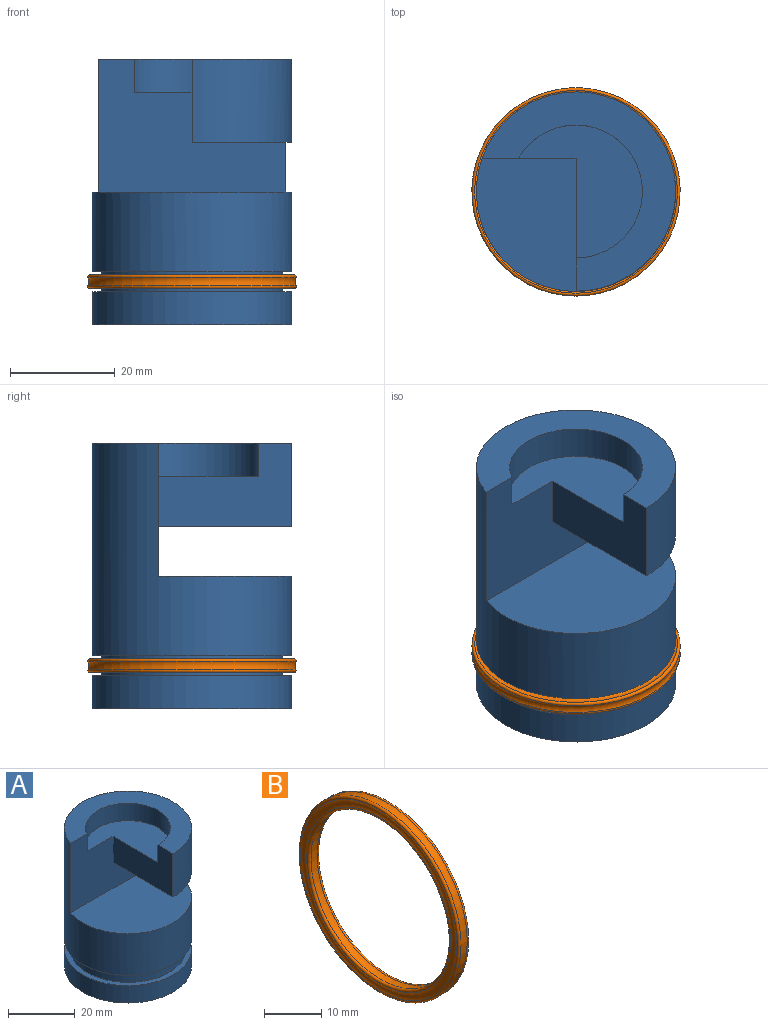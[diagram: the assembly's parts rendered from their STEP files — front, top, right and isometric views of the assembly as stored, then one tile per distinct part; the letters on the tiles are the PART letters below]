
ASSEMBLY  parts=2 mates=2
PART A: 21 faces, bbox 38.1x38.1x50.8 mm
  f0: cylinder r=19.05mm len=38.1mm, axis (0,0,-1), area 760.1mm2, adj f1,f12
  f1: plane 38.1x38.1mm, normal (0,0,-1), area 633.4mm2, adj f0,f2,f4,f6,f8
  f2: cylinder r=6.35mm len=12.7mm, axis (0,0,-1), area 63.3mm2, adj f1,f3
  f3: plane 12.7x12.7mm, normal (0,0,-1), area 126.7mm2, adj f2
  f4: cylinder r=6.35mm len=12.7mm, axis (0,0,-1), area 63.3mm2, adj f1,f5
  f5: plane 12.7x12.7mm, normal (0,0,-1), area 126.7mm2, adj f4
  f6: cylinder r=6.35mm len=12.7mm, axis (0,0,-1), area 63.3mm2, adj f1,f7
  f7: plane 12.7x12.7mm, normal (0,0,-1), area 126.7mm2, adj f6
  f8: cylinder r=6.35mm len=12.7mm, axis (0,0,-1), area 63.3mm2, adj f1,f9
  f9: plane 12.7x12.7mm, normal (0,0,-1), area 126.7mm2, adj f8
  f10: cylinder r=17.34mm len=34.67mm, axis (0,0,-1), area 415mm2, adj f11,f12
  f11: plane 38.1x38.1mm, normal (0,0,-1), area 196mm2, adj f10,f20
  f12: plane 38.1x38.1mm, normal (0,0,1), area 196mm2, adj f0,f10
  f13: cylinder r=12.7mm len=25.4mm, axis (0,0,1), area 337.8mm2, adj f14,f15,f16,f18
  f14: plane 25.4x23.7mm, normal (0,0,1), area 302.9mm2, adj f13,f15,f18
  f15: plane 25.4x15.88mm, normal (-1,0,0), area 282.3mm2, adj f13,f14,f16,f18,f19,f20
  f16: plane 38.1x37.01mm, normal (0,0,1), area 433.5mm2, adj f13,f15,f18,f20
  f17: plane 38.1x25.4mm, normal (0,0,1), area 807.4mm2, adj f18,f20
  f18: plane 35.92x25.4mm, normal (0,-1,0), area 557.4mm2, adj f13,f14,f15,f16,f17,f19,f20
  f19: plane 25.4x19.05mm, normal (0,0,-1), area 403.7mm2, adj f15,f18,f20
  f20: cylinder r=19.05mm len=40.64mm, axis (0,0,-1), area 3593.2mm2, adj f11,f15,f16,f17,f18,f19
PART B: 8 faces, bbox 3.3x43.9x43.9 mm
  f0: torus R=19.53mm, axis (-1,0,0), area 114.4mm2, adj f1,f7
  f1: torus R=21.61mm, axis (-1,0,0), area 196.9mm2, adj f0,f2
  f2: torus R=19.53mm, axis (-1,0,0), area 114.4mm2, adj f1,f3
  f3: torus R=18.61mm, axis (-1,0,0), area 185.2mm2, adj f2,f4
  f4: torus R=17.68mm, axis (-1,0,0), area 101.2mm2, adj f3,f5
  f5: torus R=15.6mm, axis (-1,0,0), area 173.6mm2, adj f4,f6
  f6: torus R=17.68mm, axis (-1,0,0), area 101.2mm2, adj f5,f7
  f7: torus R=18.61mm, axis (-1,0,0), area 185.2mm2, adj f0,f6
PLACE A t=(-27.43,-22.04,5.27)mm
PLACE B rot(axis=(0,-1,0),90deg) t=(-27.43,-22.04,13.53)mm
MATE planar A.f0 <-> B.f0  axis (0,0,-1) through (-27.43,-22.04,5.27)mm
MATE cylindrical A.f0 <-> B.f0  axis (0,0,-1) through (-27.43,-22.04,5.27)mm
